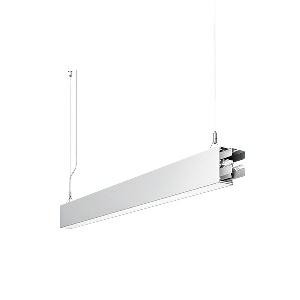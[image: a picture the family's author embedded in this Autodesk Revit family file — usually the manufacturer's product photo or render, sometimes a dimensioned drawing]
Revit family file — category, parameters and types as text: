
# Revit family: dotoo_line_-_dlp_1500_840_d_sta_00805777_efc2
name_source: partatom
category: Lighting Fixtures
units: mm (PartAtom-declared; Revit-internal decimal feet)

## family parameters
Cut with Voids When Loaded = No
Host = Face
Light Source = No
Part Type = Normal
Room Calculation Point = No
Round Connector Dimension = Use Diameter
Shared = No

## types (1)
- DOTOO.line - DLP 1500/840/D STA (1 x LED, 1350 lm, 4000K)
    Apparent Load = 13 VA
    Approval mark = CE
    CIE Flux Codes = 67 91 98 100 100
    Color Rendering = 80-89
    Color Temperature = 4000K
    Control Gear = Electronic ballast
    Default Elevation = 1800 mm
    Description = DLP 1500/840/D|Suspended luminaire|light source: LED|connected load: 220-240 V, 50/60 Hz|Power consumption: approx. 13 W|standby: approx. 0,20|luminous flux: 1350 lm|luminous efficacy: 103 lm/W|light distribution: Direct|direct ratio: approx. 100 %|colour temperature: Cold white, ca. 4000 K|color rendering index (CRI): >= 80|chromaticity tolerance:  3 SDCM|System of protection: IP 40|technology: Continuously dimmable|luminaire body|material: Sectional aluminium|colour: White|lamp cover: Acrylic (PMMA), Clear|mains lead: 2.00 m With free stranded wires|Fastening: Steel cable 0.3 - 0.7 m|glare control: Prism aperture|luminance(L65): <= 3000 cd/m|unified glare rating(4H 8H): <=  19|special features: DALI Load 1x, TouchDIM - dimming via standard switch, Through-wired, up to 18 m on one mains connection, Flicker-free, Suitable as emergency lighting, Start luminaire with mains connection, Mechanical and electrical connection of the individual modules without tools|
    Frequency = 50 Hz
    Height = 110 mm
    Lamp = 1 x LED
    Lamp Light Flux = 1350 lm
    Lamp count = 1
    Length = 1128 mm
    Luminous efficacy = 104 lm/W
    Manufacturer = Waldmann
    ModVariant = No
    Model = 00805777
    Mounting Place = Ceiling
    Mounting Type = Pendant
    Number of Poles = 1
    OnlyDefault = Yes
    Power Factor = 1
    Product Name = DOTOO.line - DLP 1500/840/D STA
    Product group = Suspended luminaire
    ProductGroupID = 9
    Protection Class = Protection class I
    Protection Degree = IP 40
    RLX_Detail_Level = 1
    RLX_Emergency_Light_Flux = 0 lm
    RLX_Emergency_Type = 0
    RLX_Emergency_Type_DB = No
    RlxData = <blob elided: 21009 chars, md5=5cc7fad2>
    Socket = socket
    Standby Power = 0 W
    System Light Flux = 1350 lm
    System Power = 13 W
    Type Comments = Product without accessories
    Type Image = 113301000-00692567.jpg
    URL = http://relux.com
    VarID = ---
    Voltage = 230 V
    Voltage Range = 220-240 V
    Weight = 0.00 kg
    Width = 60 mm  [stored 0.19685 ft]

note: [stored X ft] marks values corroborated as IEEE doubles in the binary element streams (Revit-internal decimal feet)

## geometry (parser evidence)
native form markers: Blend x4, Sweep x11
no freeform markers — native parametric forms only
